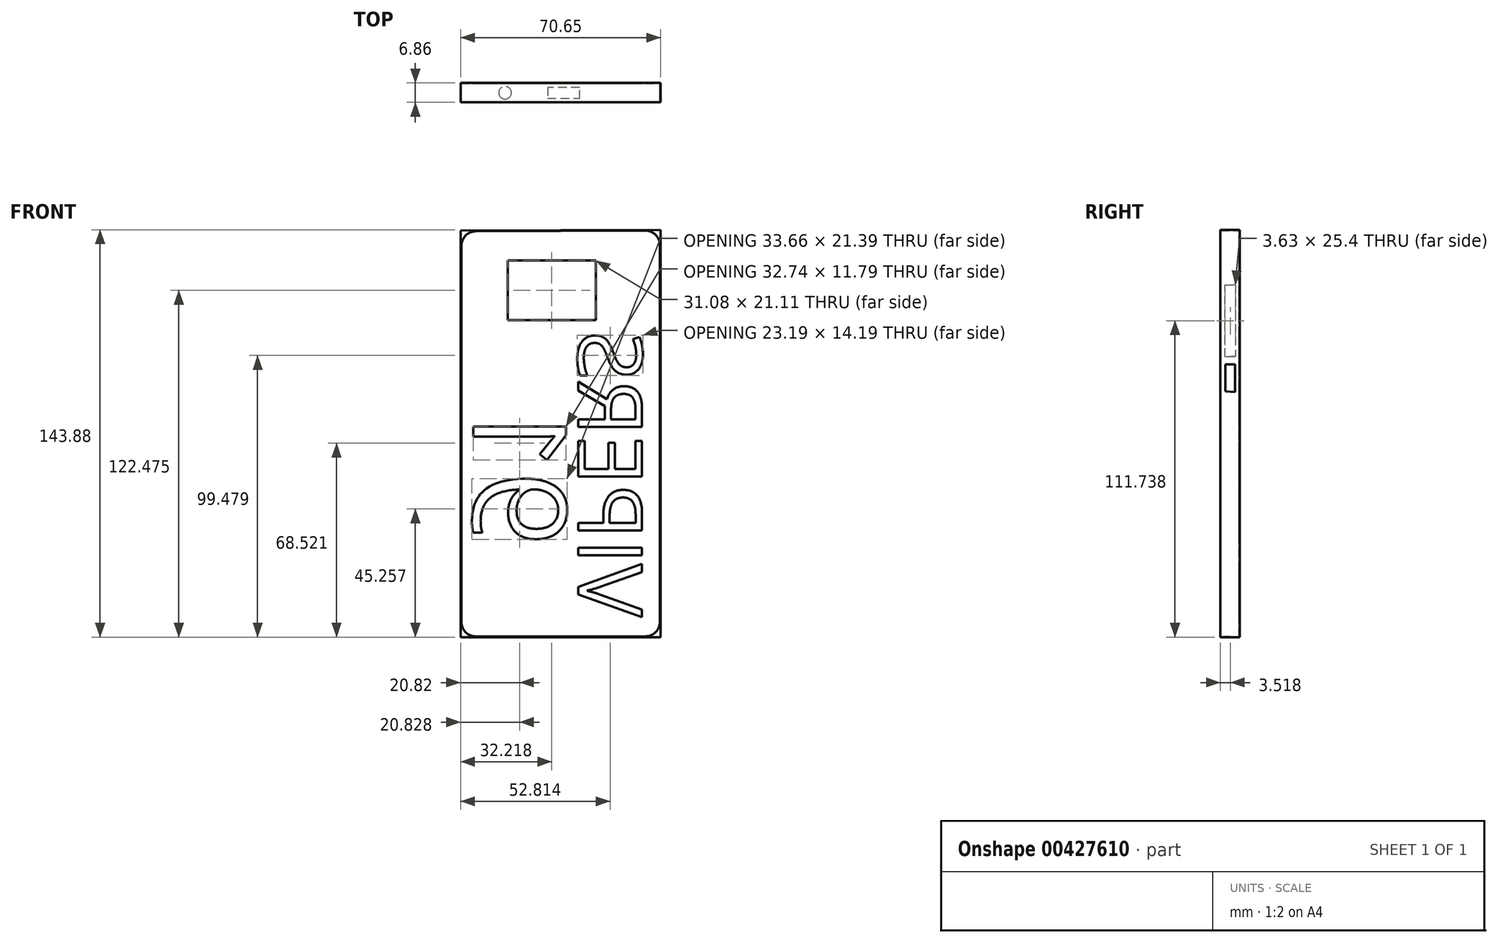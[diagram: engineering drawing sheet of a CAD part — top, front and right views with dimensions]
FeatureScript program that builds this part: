
annotation { "Feature Type Name" : "Feature", "Feature Type Description" : "" }
export const myFeature = defineFeature(function(context is Context, id is Id, definition is map)
    precondition{}
    {
        {
            var Q0;
            Q0=qCreatedBy(makeId("Front.planeOp"),FACE);
            var sketch = newSketch(context, id + "F0", { "sketchPlane" : qUnion([Q0])});
            skLineSegment(sketch, "E0", {"start": v(-45.85, 70.49) * mm, "end": v(-45.85, -73.07) * mm});
            skLineSegment(sketch, "E1", {"start": v(-45.85, -73.07) * mm, "end": v(24.8, -73.07) * mm});
            skLineSegment(sketch, "E2", {"start": v(24.8, -73.07) * mm, "end": v(24.8, 70.8) * mm});
            skLineSegment(sketch, "E3", {"start": v(24.8, 70.8) * mm, "end": v(-45.85, 70.49) * mm});
            skSolve(sketch);
        }
        {
            var Q0;
            Q0=makeQuery(id+"F0.imprint","IMPRINT",FACE,{"disambiguationData":[TD([[makeQuery(id+"F0.imprint","IMPRINT",EDGE,{"derivedFrom":sQuery(id+"F0.wireOp",EDGE,"E0")}),1.0]])]});
            extrude(context, id + "F1", {"entities" : qUnion([Q0]), "depth" : 6.86 * mm});
        }
        {
            var Q0;
            Q0=makeQuery(id+"F1.opExtrude","CAP_FACE",FACE,{"disambiguationData":[OSD([sQuery(id+"F0.wireOp",EDGE,"E0"),sQuery(id+"F0.wireOp",EDGE,"E1"),sQuery(id+"F0.wireOp",EDGE,"E2"),sQuery(id+"F0.wireOp",EDGE,"E3")])],"isStart":false});
            shell(context, id + "F2", {"entities" : qUnion([Q0]), "thickness" : 0.25 * mm});
        }
        {
            var Q0;
            Q0=makeQuery(id+"F2.opShell","OFFSET_EDGE",EDGE,{"disambiguationData":[OSD([sQuery(id+"F0.wireOp",EDGE,"E0"),sQuery(id+"F0.wireOp",EDGE,"E1")])]});
            var Q1;
            Q1=makeQuery(id+"F2.opShell","OFFSET_EDGE",EDGE,{"disambiguationData":[OSD([sQuery(id+"F0.wireOp",EDGE,"E0"),sQuery(id+"F0.wireOp",EDGE,"E3")])]});
            var Q2;
            Q2=makeQuery(id+"F2.opShell","OFFSET_EDGE",EDGE,{"disambiguationData":[OSD([sQuery(id+"F0.wireOp",EDGE,"E2"),sQuery(id+"F0.wireOp",EDGE,"E3")])]});
            fillet(context, id + "F3", {"entities" : qUnion([Q0, Q1, Q2]), "radius" : 5.08 * mm, "tangentPropagation" : true, "allowEdgeOverflow" : false});
        }
        {
            var Q0;
            Q0=makeQuery(id+"F2.opShell","OFFSET_EDGE",EDGE,{"disambiguationData":[OSD([sQuery(id+"F0.wireOp",EDGE,"E1"),sQuery(id+"F0.wireOp",EDGE,"E2")])]});
            fillet(context, id + "F4", {"entities" : qUnion([Q0]), "radius" : 5.08 * mm, "tangentPropagation" : true, "allowEdgeOverflow" : false});
        }
        {
            var Q0;
            Q0=makeQuery(id+"F1.opExtrude","CAP_FACE",FACE,{"disambiguationData":[OSD([sQuery(id+"F0.wireOp",EDGE,"E0"),sQuery(id+"F0.wireOp",EDGE,"E1"),sQuery(id+"F0.wireOp",EDGE,"E2"),sQuery(id+"F0.wireOp",EDGE,"E3")])],"isStart":true});
            var sketch = newSketch(context, id + "F5", { "sketchPlane" : qUnion([Q0])});
            skLineSegment(sketch, "E4", {"start": v(-1.9, 38.85) * mm, "end": v(29.17, 38.95) * mm});
            skLineSegment(sketch, "E5", {"start": v(-1.9, 59.96) * mm, "end": v(29.17, 59.96) * mm});
            skLineSegment(sketch, "E6", {"start": v(-1.9, 59.96) * mm, "end": v(-1.9, 38.85) * mm});
            skLineSegment(sketch, "E7", {"start": v(29.17, 59.96) * mm, "end": v(29.17, 38.95) * mm});
            skSolve(sketch);
        }
        {
            var Q0;
            Q0=makeQuery(id+"F5.imprint","IMPRINT",FACE,{"disambiguationData":[TD([[makeQuery(id+"F5.imprint","IMPRINT",EDGE,{"derivedFrom":sQuery(id+"F5.wireOp",EDGE,"E4")}),1.0]])]});
            extrude(context, id + "F6", {"entities" : qUnion([Q0]), "operationType" : NewBodyOperationType.REMOVE, "endBound" : BoundingType.THROUGH_ALL, "oppositeDirection" : true, "depth" : 25.4 * mm});
        }
        {
            var Q0;
            Q0=makeQuery(id+"F1.opExtrude","SWEPT_FACE",FACE,{"disambiguationData":[OSD([sQuery(id+"F0.wireOp",EDGE,"E2")])]});
            var sketch = newSketch(context, id + "F7", { "sketchPlane" : qUnion([Q0])});
            skLineSegment(sketch, "E8", {"start": v(-3.43, 23.26) * mm, "end": v(-5.13, 23.26) * mm});
            skLineSegment(sketch, "E9", {"start": v(-5.13, 23.26) * mm, "end": v(-5.13, 13.73) * mm});
            skLineSegment(sketch, "E10", {"start": v(-5.13, 13.73) * mm, "end": v(-1.64, 13.56) * mm});
            skLineSegment(sketch, "E11", {"start": v(-1.64, 13.56) * mm, "end": v(-1.64, 23.26) * mm});
            skLineSegment(sketch, "E12", {"start": v(-1.64, 23.26) * mm, "end": v(-5.13, 23.26) * mm});
            skSolve(sketch);
        }
        {
            var Q0;
            Q0 = qSketchRegion(id + "F7", true);
            extrude(context, id + "F8", {"entities" : qUnion([Q0]), "operationType" : NewBodyOperationType.REMOVE, "oppositeDirection" : true, "depth" : 25.4 * mm});
        }
        {
            var Q0;
            Q0=makeQuery(id+"F1.opExtrude","SWEPT_FACE",FACE,{"disambiguationData":[OSD([sQuery(id+"F0.wireOp",EDGE,"E0")])]});
            var sketch = newSketch(context, id + "F9", { "sketchPlane" : qUnion([Q0])});
            skLineSegment(sketch, "E13", {"start": v(3.43, 25.97) * mm, "end": v(5.16, 25.97) * mm});
            skLineSegment(sketch, "E14", {"start": v(5.16, 25.97) * mm, "end": v(5.16, 51.37) * mm});
            skLineSegment(sketch, "E15", {"start": v(5.16, 51.37) * mm, "end": v(1.53, 51.37) * mm});
            skLineSegment(sketch, "E16", {"start": v(1.53, 51.37) * mm, "end": v(1.53, 26.16) * mm});
            skLineSegment(sketch, "E17", {"start": v(1.53, 26.16) * mm, "end": v(5.16, 25.97) * mm});
            skSolve(sketch);
        }
        {
            var Q0;
            Q0 = qSketchRegion(id + "F9", true);
            extrude(context, id + "F10", {"entities" : qUnion([Q0]), "operationType" : NewBodyOperationType.REMOVE, "oppositeDirection" : true, "depth" : 25.4 * mm});
        }
        {
            var Q0;
            Q0=makeQuery(id+"F1.opExtrude","SWEPT_FACE",FACE,{"disambiguationData":[OSD([sQuery(id+"F0.wireOp",EDGE,"E1")])]});
            var sketch = newSketch(context, id + "F11", { "sketchPlane" : qUnion([Q0])});
            skCircle(sketch, "E18", {"center": v(-30.13, 3.43) * mm, "radius": 2.22 * mm});
            skLineSegment(sketch, "E19", {"start": v(-15.13, 3.43) * mm, "end": v(-15.13, 5.46) * mm});
            skLineSegment(sketch, "E20", {"start": v(-15.13, 5.46) * mm, "end": v(-3.8, 5.46) * mm});
            skLineSegment(sketch, "E21", {"start": v(-3.8, 5.46) * mm, "end": v(-3.8, 1.59) * mm});
            skLineSegment(sketch, "E22", {"start": v(-3.8, 1.59) * mm, "end": v(-15.13, 1.59) * mm});
            skLineSegment(sketch, "E23", {"start": v(-15.13, 1.59) * mm, "end": v(-15.13, 5.46) * mm});
            skSolve(sketch);
        }
        {
            var Q0;
            Q0 = qSketchRegion(id + "F11", true);
            extrude(context, id + "F12", {"entities" : qUnion([Q0]), "operationType" : NewBodyOperationType.REMOVE, "oppositeDirection" : true, "depth" : 25.4 * mm});
        }
        {
            var Q0;
            Q0 = qSketchRegion(id + "F11", true);
            extrude(context, id + "F13", {"entities" : qUnion([Q0]), "operationType" : NewBodyOperationType.REMOVE, "oppositeDirection" : true, "depth" : 25.4 * mm});
        }
        {
            var Q0;
            Q0=makeQuery(id+"F1.opExtrude","CAP_FACE",FACE,{"disambiguationData":[OSD([sQuery(id+"F0.wireOp",EDGE,"E0"),sQuery(id+"F0.wireOp",EDGE,"E1"),sQuery(id+"F0.wireOp",EDGE,"E2"),sQuery(id+"F0.wireOp",EDGE,"E3")])],"isStart":true});
            var sketch = newSketch(context, id + "F14", { "sketchPlane" : qUnion([Q0])});
            skText(sketch, "E24", { "text": "VIPERS", "fontName": "OpenSans-Regular.ttf"});
            skText(sketch, "E25", { "text": "91", "fontName": "OpenSans-Regular.ttf"});
            const initialGuessF14  = {"E24": [0.00432, -0.06606, 0, 1, 0.02275], "E25": [0.0414, -0.04088, 0, 1, 0.03302]};
            skSetInitialGuess(sketch, initialGuessF14);
            skSolve(sketch);
        }
        {
            var Q0;
            Q0 = qSketchRegion(id + "F14", true);
            extrude(context, id + "F15", {"entities" : qUnion([Q0]), "operationType" : NewBodyOperationType.REMOVE, "oppositeDirection" : true, "depth" : 25.4 * mm});
        }
        {
            var Q0;
            Q0 = qSketchRegion(id + "F14", true);
            extrude(context, id + "F16", {"entities" : qUnion([Q0]), "operationType" : NewBodyOperationType.REMOVE, "oppositeDirection" : true, "depth" : 25.4 * mm});
        }
    });
